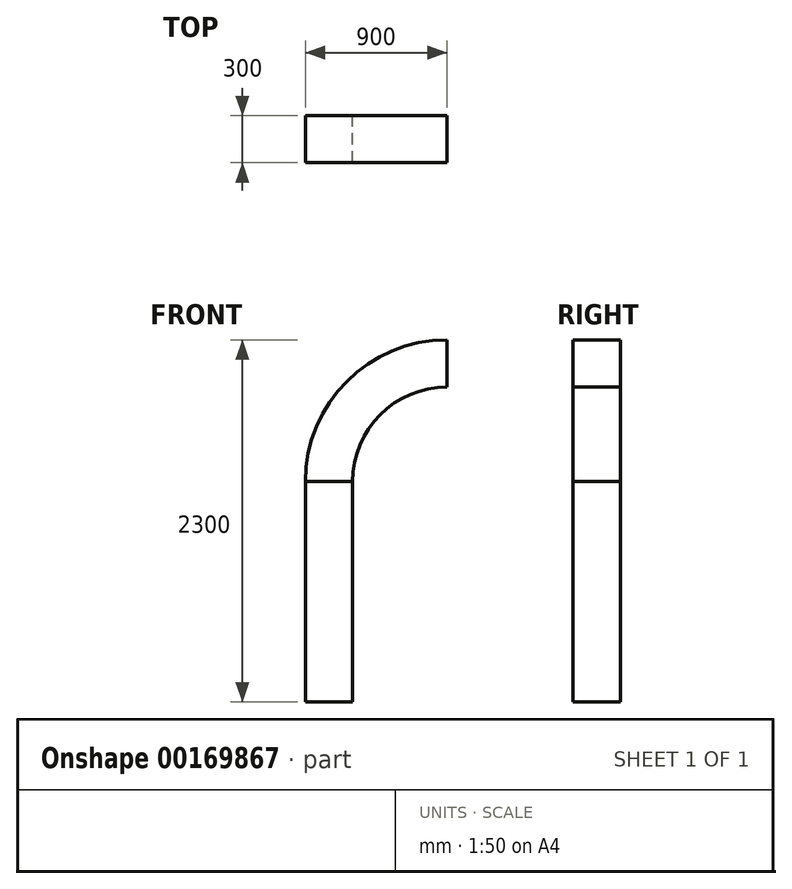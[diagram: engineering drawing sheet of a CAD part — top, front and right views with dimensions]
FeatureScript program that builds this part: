
annotation { "Feature Type Name" : "Feature", "Feature Type Description" : "" }
export const myFeature = defineFeature(function(context is Context, id is Id, definition is map)
    precondition{}
    {
        {
            var Q0;
            Q0=qCreatedBy(makeId("Front.planeOp"),FACE);
            var sketch = newSketch(context, id + "F0", { "sketchPlane" : qUnion([Q0])});
            skLineSegment(sketch, "E0", {"start": v(0, 0) * mm, "end": v(0, 2000) * mm, "construction": true});
            skLineSegment(sketch, "E1", {"start": v(0, 0) * mm, "end": v(-600, 0) * mm, "construction": true});
            skLineSegment(sketch, "E2", {"start": v(-600, 0) * mm, "end": v(-600, 1400) * mm});
            skArc(sketch, "E3", {"start": v(0, 2000) * mm, "mid": v(-424.26, 1824.26) * mm, "end": v(-600, 1400) * mm});
            skArc(sketch, "E4.0", {"start": v(0, 2300) * mm, "mid": v(-636.4, 2036.4) * mm, "end": v(-900, 1400) * mm});
            skLineSegment(sketch, "E4.1", {"start": v(-900, 0) * mm, "end": v(-900, 1400) * mm});
            skLineSegment(sketch, "E5", {"start": v(-600, 0) * mm, "end": v(-900, 0) * mm});
            skLineSegment(sketch, "E6", {"start": v(-600, 1400) * mm, "end": v(-900, 1400) * mm});
            skLineSegment(sketch, "E7", {"start": v(0, 2300) * mm, "end": v(0, 2000) * mm});
            skSolve(sketch);
        }
        {
            var Q0;
            Q0=makeQuery(id+"F0.imprint","IMPRINT",FACE,{"disambiguationData":[TD([[makeQuery(id+"F0.imprint","IMPRINT",EDGE,{"derivedFrom":sQuery(id+"F0.wireOp",EDGE,"E2")}),1.0]])]});
            extrude(context, id + "F1", {"entities" : qUnion([Q0]), "depth" : 300 * mm});
        }
        {
            var Q0;
            {var subQ0=sQuery(id+"F0.wireOp",EDGE,"E6");Q0=makeQuery(id+"F0.imprint","IMPRINT",FACE,{"disambiguationData":[TD([[makeQuery(id+"F0.imprint","IMPRINT",EDGE,{"derivedFrom":subQ0}),-1.0]])]});}
            extrude(context, id + "F2", {"entities" : qUnion([Q0]), "depth" : 300 * mm});
        }
    });
